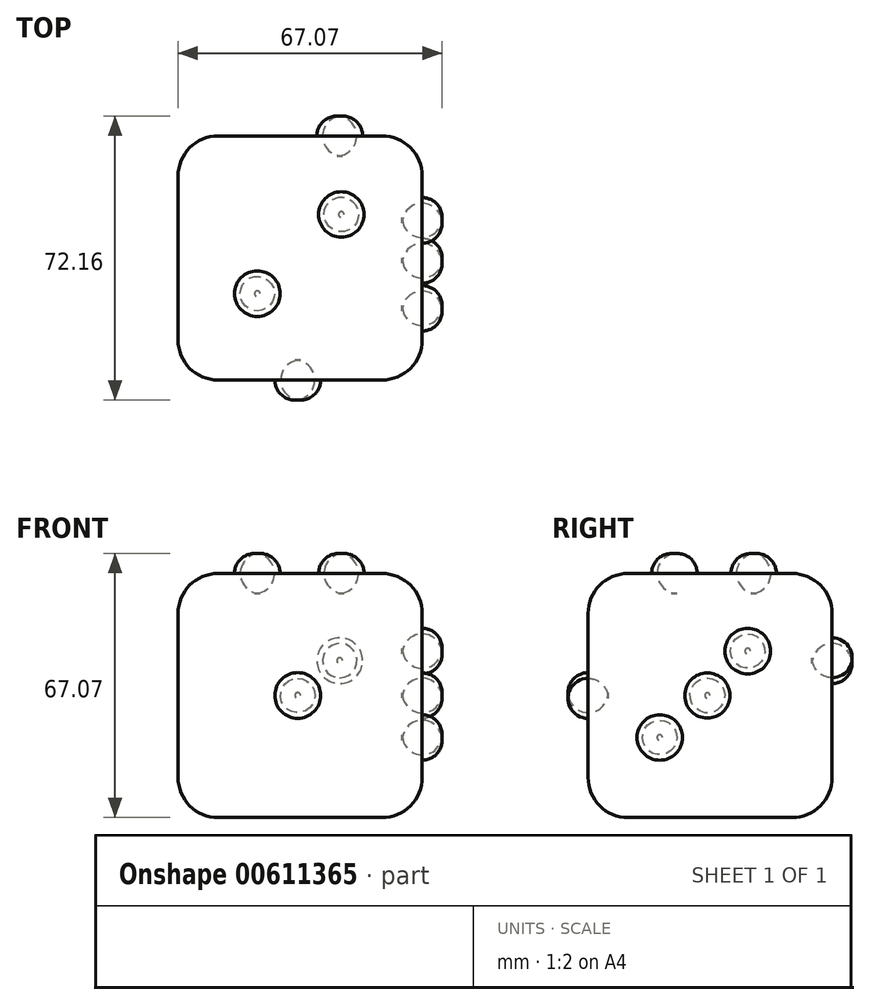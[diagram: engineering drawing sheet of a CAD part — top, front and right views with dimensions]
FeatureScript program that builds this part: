
annotation { "Feature Type Name" : "Feature", "Feature Type Description" : "" }
export const myFeature = defineFeature(function(context is Context, id is Id, definition is map)
    precondition{}
    {
        {
            var Q0;
            Q0=qCreatedBy(makeId("Front.planeOp"),FACE);
            var sketch = newSketch(context, id + "F0", { "sketchPlane" : qUnion([Q0])});
            skLineSegment(sketch, "E0.bottom", {"start": v(-47.2, 27.17) * mm, "end": v(14.8, 27.17) * mm});
            skLineSegment(sketch, "E0.top", {"start": v(-47.2, -34.82) * mm, "end": v(14.8, -34.82) * mm});
            skLineSegment(sketch, "E0.left", {"start": v(-47.2, 27.17) * mm, "end": v(-47.2, -34.82) * mm});
            skLineSegment(sketch, "E0.right", {"start": v(14.8, 27.17) * mm, "end": v(14.8, -34.82) * mm});
            skSolve(sketch);
        }
        {
            var Q0;
            Q0 = qSketchRegion(id + "F0", true);
            extrude(context, id + "F1", {"entities" : qUnion([Q0]), "depth" : 62 * mm, "offsetDistance" : 25.4 * mm});
        }
        {
            var Q0;
            Q0=makeQuery(id+"F1.opExtrude","CAP_EDGE",EDGE,{"disambiguationData":[OSD([sQuery(id+"F0.wireOp",EDGE,"E0.bottom")])],"isStart":false});
            var Q1;
            Q1=makeQuery(id+"F1.opExtrude","CAP_EDGE",EDGE,{"disambiguationData":[OSD([sQuery(id+"F0.wireOp",EDGE,"E0.right")])],"isStart":false});
            var Q2;
            Q2=makeQuery(id+"F1.opExtrude","CAP_EDGE",EDGE,{"disambiguationData":[OSD([sQuery(id+"F0.wireOp",EDGE,"E0.left")])],"isStart":false});
            var Q3;
            Q3=makeQuery(id+"F1.opExtrude","CAP_EDGE",EDGE,{"disambiguationData":[OSD([sQuery(id+"F0.wireOp",EDGE,"E0.top")])],"isStart":false});
            var Q4;
            Q4=makeQuery(id+"F1.opExtrude","SWEPT_EDGE",EDGE,{"disambiguationData":[OSD([sQuery(id+"F0.wireOp",EDGE,"E0.top"),sQuery(id+"F0.wireOp",EDGE,"E0.right")])]});
            var Q5;
            Q5=makeQuery(id+"F1.opExtrude","SWEPT_EDGE",EDGE,{"disambiguationData":[OSD([sQuery(id+"F0.wireOp",EDGE,"E0.bottom"),sQuery(id+"F0.wireOp",EDGE,"E0.right")])]});
            var Q6;
            Q6=makeQuery(id+"F1.opExtrude","CAP_EDGE",EDGE,{"disambiguationData":[OSD([sQuery(id+"F0.wireOp",EDGE,"E0.right")])],"isStart":true});
            var Q7;
            Q7=makeQuery(id+"F1.opExtrude","CAP_EDGE",EDGE,{"disambiguationData":[OSD([sQuery(id+"F0.wireOp",EDGE,"E0.bottom")])],"isStart":true});
            var Q8;
            Q8=makeQuery(id+"F1.opExtrude","SWEPT_EDGE",EDGE,{"disambiguationData":[OSD([sQuery(id+"F0.wireOp",EDGE,"E0.bottom"),sQuery(id+"F0.wireOp",EDGE,"E0.left")])]});
            var Q9;
            Q9=makeQuery(id+"F1.opExtrude","CAP_EDGE",EDGE,{"disambiguationData":[OSD([sQuery(id+"F0.wireOp",EDGE,"E0.left")])],"isStart":true});
            var Q10;
            Q10=makeQuery(id+"F1.opExtrude","SWEPT_EDGE",EDGE,{"disambiguationData":[OSD([sQuery(id+"F0.wireOp",EDGE,"E0.top"),sQuery(id+"F0.wireOp",EDGE,"E0.left")])]});
            var Q11;
            Q11=makeQuery(id+"F1.opExtrude","CAP_EDGE",EDGE,{"disambiguationData":[OSD([sQuery(id+"F0.wireOp",EDGE,"E0.top")])],"isStart":true});
            fillet(context, id + "F2", {"entities" : qUnion([Q0, Q1, Q2, Q3, Q4, Q5, Q6, Q7, Q8, Q9, Q10, Q11]), "radius" : 10.16 * mm, "tangentPropagation" : true, "allowEdgeOverflow" : false});
        }
        {
            var Q0;
            Q0=makeQuery(id+"F1.opExtrude","CAP_FACE",FACE,{"disambiguationData":[OSD([sQuery(id+"F0.wireOp",EDGE,"E0.bottom"),sQuery(id+"F0.wireOp",EDGE,"E0.top"),sQuery(id+"F0.wireOp",EDGE,"E0.left"),sQuery(id+"F0.wireOp",EDGE,"E0.right")])],"isStart":false});
            var sketch = newSketch(context, id + "F3", { "sketchPlane" : qUnion([Q0])});
            skCircle(sketch, "E1", {"center": v(-16.8, -3.82) * mm, "radius": 5.8 * mm});
            skPoint(sketch, "E1.centerSnap0", {"position": v(-37.04, -3.82) * mm});
            skSolve(sketch);
        }
        {
            var Q0;
            Q0 = qSketchRegion(id + "F3", true);
            extrude(context, id + "F4", {"entities" : qUnion([Q0]), "operationType" : NewBodyOperationType.REMOVE, "oppositeDirection" : true, "depth" : 5.08 * mm, "offsetDistance" : 25.4 * mm});
        }
        {
            var Q0;
            Q0=makeQuery(id+"F4.boolean.opBoolean","COPY",EDGE,{"derivedFrom":makeQuery(id+"F4.opExtrude","CAP_EDGE",EDGE,{"disambiguationData":[OSD([sQuery(id+"F3.wireOp",EDGE,"E1")])],"isStart":false})});
            fillet(context, id + "F5", {"entities" : qUnion([Q0]), "radius" : 5.08 * mm, "tangentPropagation" : true, "allowEdgeOverflow" : false});
        }
        {
            var Q0;
            Q0=makeQuery(id+"F1.opExtrude","SWEPT_FACE",FACE,{"disambiguationData":[OSD([sQuery(id+"F0.wireOp",EDGE,"E0.bottom")])]});
            var sketch = newSketch(context, id + "F6", { "sketchPlane" : qUnion([Q0])});
            skCircle(sketch, "E2", {"center": v(-27.07, -40.06) * mm, "radius": 5.8 * mm});
            skSolve(sketch);
        }
        {
            var Q0;
            Q0=makeQuery(id+"F6.imprint","IMPRINT",FACE,{"disambiguationData":[TD([[makeQuery(id+"F6.imprint","IMPRINT",EDGE,{"derivedFrom":sQuery(id+"F6.wireOp",EDGE,"E2")}),1.0]])]});
            extrude(context, id + "F7", {"entities" : qUnion([Q0]), "operationType" : NewBodyOperationType.REMOVE, "oppositeDirection" : true, "depth" : 5.08 * mm, "offsetDistance" : 25.4 * mm});
        }
        {
            var Q0;
            Q0=makeQuery(id+"F7.boolean.opBoolean","COPY",FACE,{"derivedFrom":makeQuery(id+"F7.opExtrude","CAP_FACE",FACE,{"disambiguationData":[OSD([sQuery(id+"F6.wireOp",EDGE,"E2")])],"isStart":false})});
            fillet(context, id + "F8", {"entities" : qUnion([Q0]), "radius" : 5.08 * mm, "tangentPropagation" : true, "allowEdgeOverflow" : false});
        }
        {
            var Q0;
            Q0=makeQuery(id+"F1.opExtrude","SWEPT_FACE",FACE,{"disambiguationData":[OSD([sQuery(id+"F0.wireOp",EDGE,"E0.bottom")])]});
            var sketch = newSketch(context, id + "F9", { "sketchPlane" : qUnion([Q0])});
            skCircle(sketch, "E3", {"center": v(-5.74, -19.93) * mm, "radius": 5.77 * mm});
            skSolve(sketch);
        }
        {
            var Q0;
            Q0=makeQuery(id+"F9.imprint","IMPRINT",FACE,{"disambiguationData":[TD([[makeQuery(id+"F9.imprint","IMPRINT",EDGE,{"derivedFrom":sQuery(id+"F9.wireOp",EDGE,"E3")}),1.0]])]});
            extrude(context, id + "F10", {"entities" : qUnion([Q0]), "operationType" : NewBodyOperationType.REMOVE, "oppositeDirection" : true, "depth" : 5.08 * mm, "offsetDistance" : 25.4 * mm});
        }
        {
            var Q0;
            Q0=makeQuery(id+"F10.boolean.opBoolean","COPY",FACE,{"derivedFrom":makeQuery(id+"F10.opExtrude","CAP_FACE",FACE,{"disambiguationData":[OSD([sQuery(id+"F9.wireOp",EDGE,"E3")])],"isStart":false})});
            fillet(context, id + "F11", {"entities" : qUnion([Q0]), "radius" : 5.08 * mm, "tangentPropagation" : true, "allowEdgeOverflow" : false});
        }
        {
            var Q0;
            Q0=makeQuery(id+"F1.opExtrude","SWEPT_FACE",FACE,{"disambiguationData":[OSD([sQuery(id+"F0.wireOp",EDGE,"E0.right")])]});
            var sketch = newSketch(context, id + "F12", { "sketchPlane" : qUnion([Q0])});
            skCircle(sketch, "E4", {"center": v(-21.44, 7.45) * mm, "radius": 5.8 * mm});
            skSolve(sketch);
        }
        {
            var Q0;
            Q0=makeQuery(id+"F12.imprint","IMPRINT",FACE,{"disambiguationData":[TD([[makeQuery(id+"F12.imprint","IMPRINT",EDGE,{"derivedFrom":sQuery(id+"F12.wireOp",EDGE,"E4")}),1.0]])]});
            extrude(context, id + "F13", {"entities" : qUnion([Q0]), "operationType" : NewBodyOperationType.REMOVE, "oppositeDirection" : true, "depth" : 5.08 * mm, "offsetDistance" : 25.4 * mm});
        }
        {
            var Q0;
            Q0=makeQuery(id+"F13.boolean.opBoolean","COPY",FACE,{"derivedFrom":makeQuery(id+"F13.opExtrude","CAP_FACE",FACE,{"disambiguationData":[OSD([sQuery(id+"F12.wireOp",EDGE,"E4")])],"isStart":false})});
            fillet(context, id + "F14", {"entities" : qUnion([Q0]), "radius" : 5.08 * mm, "tangentPropagation" : true, "allowEdgeOverflow" : false});
        }
        {
            var Q0;
            Q0=makeQuery(id+"F1.opExtrude","SWEPT_FACE",FACE,{"disambiguationData":[OSD([sQuery(id+"F0.wireOp",EDGE,"E0.right")])]});
            var sketch = newSketch(context, id + "F15", { "sketchPlane" : qUnion([Q0])});
            skCircle(sketch, "E5", {"center": v(-31.68, -3.82) * mm, "radius": 5.73 * mm});
            skPoint(sketch, "E5.centerSnap0", {"position": v(-10.16, -3.82) * mm});
            skSolve(sketch);
        }
        {
            var Q0;
            Q0=makeQuery(id+"F15.imprint","IMPRINT",FACE,{"disambiguationData":[TD([[makeQuery(id+"F15.imprint","IMPRINT",EDGE,{"derivedFrom":sQuery(id+"F15.wireOp",EDGE,"E5")}),1.0]])]});
            extrude(context, id + "F16", {"entities" : qUnion([Q0]), "operationType" : NewBodyOperationType.REMOVE, "oppositeDirection" : true, "depth" : 5.08 * mm, "offsetDistance" : 25.4 * mm});
        }
        {
            var Q0;
            Q0=makeQuery(id+"F16.boolean.opBoolean","COPY",FACE,{"derivedFrom":makeQuery(id+"F16.opExtrude","CAP_FACE",FACE,{"disambiguationData":[OSD([sQuery(id+"F15.wireOp",EDGE,"E5")])],"isStart":false})});
            fillet(context, id + "F17", {"entities" : qUnion([Q0]), "radius" : 5.08 * mm, "tangentPropagation" : true, "allowEdgeOverflow" : false});
        }
        {
            var Q0;
            Q0=makeQuery(id+"F1.opExtrude","SWEPT_FACE",FACE,{"disambiguationData":[OSD([sQuery(id+"F0.wireOp",EDGE,"E0.right")])]});
            var sketch = newSketch(context, id + "F18", { "sketchPlane" : qUnion([Q0])});
            skCircle(sketch, "E6", {"center": v(-43.78, -14.5) * mm, "radius": 5.77 * mm});
            skSolve(sketch);
        }
        {
            var Q0;
            Q0=makeQuery(id+"F18.imprint","IMPRINT",FACE,{"disambiguationData":[TD([[makeQuery(id+"F18.imprint","IMPRINT",EDGE,{"derivedFrom":sQuery(id+"F18.wireOp",EDGE,"E6")}),1.0]])]});
            extrude(context, id + "F19", {"entities" : qUnion([Q0]), "operationType" : NewBodyOperationType.REMOVE, "oppositeDirection" : true, "depth" : 5.08 * mm, "offsetDistance" : 25.4 * mm});
        }
        {
            var Q0;
            Q0=makeQuery(id+"F19.boolean.opBoolean","COPY",FACE,{"derivedFrom":makeQuery(id+"F19.opExtrude","CAP_FACE",FACE,{"disambiguationData":[OSD([sQuery(id+"F18.wireOp",EDGE,"E6")])],"isStart":false})});
            fillet(context, id + "F20", {"entities" : qUnion([Q0]), "radius" : 5.08 * mm, "tangentPropagation" : true, "allowEdgeOverflow" : false});
        }
        {
            var Q0;
            Q0=makeQuery(id+"F1.opExtrude","CAP_FACE",FACE,{"disambiguationData":[OSD([sQuery(id+"F0.wireOp",EDGE,"E0.bottom"),sQuery(id+"F0.wireOp",EDGE,"E0.top"),sQuery(id+"F0.wireOp",EDGE,"E0.left"),sQuery(id+"F0.wireOp",EDGE,"E0.right")])],"isStart":true});
            var sketch = newSketch(context, id + "F21", { "sketchPlane" : qUnion([Q0])});
            skCircle(sketch, "E7", {"center": v(6.14, 5.03) * mm, "radius": 5.8 * mm});
            skSolve(sketch);
        }
        {
            var Q0;
            Q0=makeQuery(id+"F21.imprint","IMPRINT",FACE,{"disambiguationData":[TD([[makeQuery(id+"F21.imprint","IMPRINT",EDGE,{"derivedFrom":sQuery(id+"F21.wireOp",EDGE,"E7")}),1.0]])]});
            extrude(context, id + "F22", {"entities" : qUnion([Q0]), "operationType" : NewBodyOperationType.REMOVE, "oppositeDirection" : true, "depth" : 5.08 * mm, "offsetDistance" : 25.4 * mm});
        }
        {
            var Q0;
            Q0=makeQuery(id+"F22.boolean.opBoolean","COPY",FACE,{"derivedFrom":makeQuery(id+"F22.opExtrude","CAP_FACE",FACE,{"disambiguationData":[OSD([sQuery(id+"F21.wireOp",EDGE,"E7")])],"isStart":false})});
            fillet(context, id + "F23", {"entities" : qUnion([Q0]), "radius" : 5.08 * mm, "tangentPropagation" : true, "allowEdgeOverflow" : false});
        }
    });
